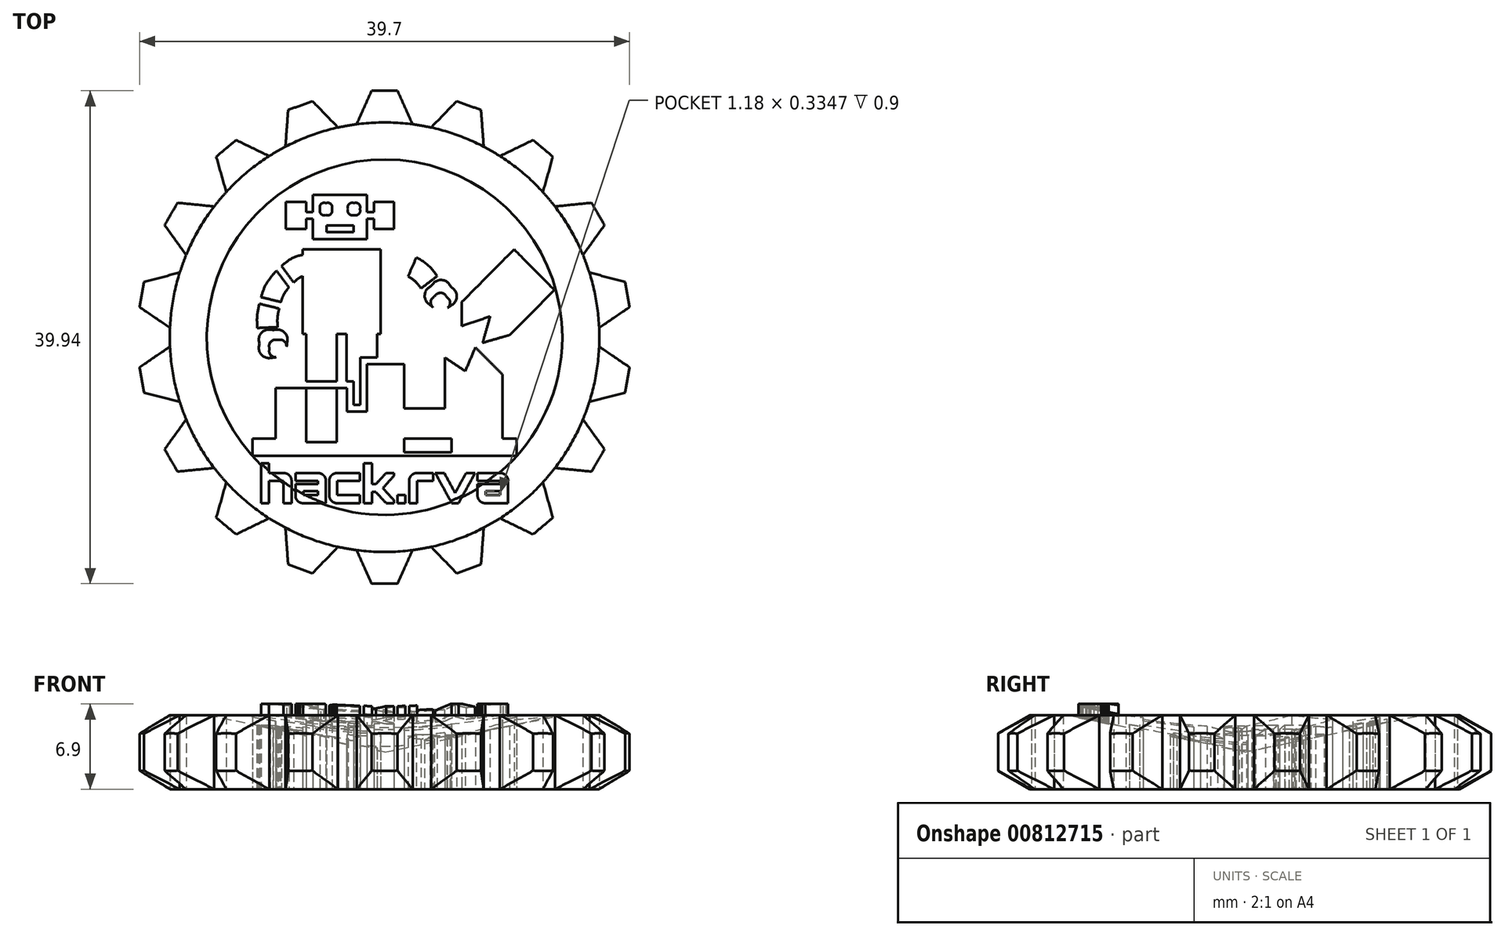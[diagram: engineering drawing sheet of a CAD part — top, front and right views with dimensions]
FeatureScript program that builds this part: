
annotation { "Feature Type Name" : "Feature", "Feature Type Description" : "" }
export const myFeature = defineFeature(function(context is Context, id is Id, definition is map)
    precondition{}
    {
        {
            var Q0;
            Q0=qCreatedBy(makeId("Top.planeOp"),FACE);
            var sketch = newSketch(context, id + "F0", { "sketchPlane" : qUnion([Q0])});
            skCircle(sketch, "E0", {"center": v(0, 0) * mm, "radius": 17.4 * mm, "construction": true});
            skCircle(sketch, "E1", {"center": v(0, 0) * mm, "radius": 20 * mm, "construction": true});
            skLineSegment(sketch, "E2", {"start": v(0, 0) * mm, "end": v(0, 27.02) * mm, "construction": true});
            skLineSegment(sketch, "E3", {"start": v(0, 0) * mm, "end": v(-2.84, 21.54) * mm, "construction": true});
            skLineSegment(sketch, "E4", {"start": v(0, 0) * mm, "end": v(-1.42, 27.06) * mm, "construction": true});
            skPoint(sketch, "E4.endSnap0", {"position": v(-1.42, 10.77) * mm});
            skLineSegment(sketch, "E5", {"start": v(-2.27, 17.25) * mm, "end": v(-1.05, 19.97) * mm});
            skLineSegment(sketch, "E6", {"start": v(-1.05, 19.97) * mm, "end": v(0, 19.97) * mm});
            skLineSegment(sketch, "E7.MirrorCS", {"start": v(2.27, 17.25) * mm, "end": v(1.05, 19.97) * mm});
            skLineSegment(sketch, "E8.MirrorCS", {"start": v(1.05, 19.97) * mm, "end": v(0, 19.97) * mm});
            skLineSegment(sketch, "E9", {"start": v(-2.27, 17.25) * mm, "end": v(2.27, 17.25) * mm});
            skSolve(sketch);
        }
        {
            var Q0;
            Q0=qCreatedBy(makeId("Top.planeOp"),FACE);
            var sketch = newSketch(context, id + "F1", { "sketchPlane" : qUnion([Q0])});
            skCircle(sketch, "E10", {"center": v(0, 0) * mm, "radius": 17.4 * mm});
            skSolve(sketch);
        }
        {
            var Q0;
            Q0=qSketchRegion(id+"F1",true);
            var Q1;
            Q1=qSketchRegion(id+"F0",true);
            extrude(context, id + "F2", {"entities" : qUnion([Q0, Q1]), "depth" : 6 * mm, "offsetDistance" : 25 * mm});
        }
        {
            var Q0;
            Q0=qCreatedBy(makeId("Front.planeOp"),FACE);
            var sketch = newSketch(context, id + "F3", { "sketchPlane" : qUnion([Q0])});
            skLineSegment(sketch, "E11", {"start": v(0, 0) * mm, "end": v(0, 3) * mm});
            skLineSegment(sketch, "E12", {"start": v(0, 3) * mm, "end": v(-14.4, 6) * mm});
            skLineSegment(sketch, "E13", {"start": v(-14.4, 6) * mm, "end": v(-17.4, 6) * mm});
            skLineSegment(sketch, "E14", {"start": v(-17.4, 6) * mm, "end": v(-20, 4.5) * mm});
            skLineSegment(sketch, "E15", {"start": v(-20, 4.5) * mm, "end": v(-20, 1.5) * mm});
            skLineSegment(sketch, "E16", {"start": v(-20, 1.5) * mm, "end": v(-17.4, 0) * mm});
            skLineSegment(sketch, "E17", {"start": v(-17.4, 0) * mm, "end": v(0, 0) * mm});
            skSolve(sketch);
        }
        {
            var Q0;
            Q0=makeQuery(id+"F2.opExtrude","SWEPT_BODY",BODY,{"disambiguationData":[OSD([sQuery(id+"F0.wireOp",EDGE,"E5"),sQuery(id+"F0.wireOp",EDGE,"E6"),sQuery(id+"F0.wireOp",EDGE,"E7.MirrorCS"),sQuery(id+"F0.wireOp",EDGE,"E8.MirrorCS"),sQuery(id+"F0.wireOp",EDGE,"E9")])]});
            var Q1;
            Q1=sQuery(id+"F3.wireOp",EDGE,"E11");
            circularPattern(context, id + "F4", {"operationType" : NewBodyOperationType.ADD, "entities" : qUnion([Q0]), "axis" : qUnion([Q1]), "angle" : 360 * degree, "instanceCount" : 18, "equalSpace" : true});
        }
        {
            var Q0;
            Q0=qCreatedBy(makeId("Top.planeOp"),FACE);
            var sketch = newSketch(context, id + "F5", { "sketchPlane" : qUnion([Q0])});
            skLineSegment(sketch, "E18", {"start": v(7.36, -0.83) * mm, "end": v(6.54, -2.75) * mm});
            skLineSegment(sketch, "E19", {"start": v(6.54, -2.75) * mm, "end": v(4.9, -1.65) * mm});
            skLineSegment(sketch, "E20", {"start": v(4.9, -1.65) * mm, "end": v(4.9, -9.06) * mm});
            skLineSegment(sketch, "E21", {"start": v(4.9, -9.06) * mm, "end": v(9.56, -9.06) * mm});
            skLineSegment(sketch, "E22", {"start": v(9.56, -9.06) * mm, "end": v(9.56, -3.02) * mm});
            skLineSegment(sketch, "E23", {"start": v(9.56, -3.02) * mm, "end": v(8.46, -1.92) * mm});
            skLineSegment(sketch, "E24", {"start": v(8.46, -1.92) * mm, "end": v(7.36, -0.83) * mm});
            skLineSegment(sketch, "E25", {"start": v(1.6, -5.77) * mm, "end": v(5.44, -5.77) * mm});
            skLineSegment(sketch, "E26", {"start": v(5.44, -5.77) * mm, "end": v(5.44, -9.33) * mm});
            skLineSegment(sketch, "E27", {"start": v(5.44, -9.33) * mm, "end": v(1.6, -9.33) * mm});
            skLineSegment(sketch, "E28", {"start": v(1.6, -9.33) * mm, "end": v(1.6, -5.77) * mm});
            skLineSegment(sketch, "E29", {"start": v(8.55, 1.69) * mm, "end": v(7.95, -0.45) * mm});
            skLineSegment(sketch, "E30", {"start": v(7.95, -0.45) * mm, "end": v(10.12, 0.17) * mm});
            skLineSegment(sketch, "E31", {"start": v(10.12, 0.17) * mm, "end": v(13.76, 3.82) * mm});
            skLineSegment(sketch, "E32", {"start": v(13.76, 3.82) * mm, "end": v(10.5, 7.12) * mm});
            skLineSegment(sketch, "E33", {"start": v(10.5, 7.12) * mm, "end": v(6.26, 2.85) * mm});
            skLineSegment(sketch, "E34", {"start": v(6.26, 2.85) * mm, "end": v(6.26, 0.9) * mm});
            skLineSegment(sketch, "E35", {"start": v(6.26, 0.9) * mm, "end": v(8.55, 1.69) * mm});
            skFitSpline(sketch, "E36", {"points": [v(-9.33, -0.94) * mm, v(-9.33, -0.55) * mm, v(-9.02, -0.23) * mm, v(-8.62, -0.23) * mm]});
            skFitSpline(sketch, "E37", {"points": [v(-8.62, -0.23) * mm, v(-8.3, -0.23) * mm, v(-8.02, -0.46) * mm, v(-7.94, -0.77) * mm]});
            skFitSpline(sketch, "E38", {"points": [v(-7.94, -0.77) * mm, v(-7.92, -0.7) * mm, v(-7.91, -0.61) * mm, v(-7.91, -0.53) * mm]});
            skFitSpline(sketch, "E39", {"points": [v(-7.91, -0.53) * mm, v(-7.91, 0.08) * mm, v(-8.41, 0.58) * mm, v(-9.03, 0.58) * mm]});
            skFitSpline(sketch, "E40", {"points": [v(-9.03, 0.58) * mm, v(-9.64, 0.58) * mm, v(-10.14, 0.08) * mm, v(-10.14, -0.53) * mm]});
            skFitSpline(sketch, "E41", {"points": [v(-10.14, -0.53) * mm, v(-10.14, -1.15) * mm, v(-9.64, -1.65) * mm, v(-9.03, -1.65) * mm]});
            skFitSpline(sketch, "E42", {"points": [v(-9.03, -1.65) * mm, v(-8.95, -1.65) * mm, v(-8.87, -1.64) * mm, v(-8.8, -1.63) * mm]});
            skFitSpline(sketch, "E43", {"points": [v(-8.8, -1.63) * mm, v(-9.1, -1.55) * mm, v(-9.33, -1.27) * mm, v(-9.33, -0.94) * mm]});
            skLineSegment(sketch, "E44", {"start": v(-1.42, 10.15) * mm, "end": v(0.77, 10.15) * mm});
            skLineSegment(sketch, "E45", {"start": v(0.77, 10.15) * mm, "end": v(0.77, 9.6) * mm});
            skLineSegment(sketch, "E46", {"start": v(0.77, 9.6) * mm, "end": v(-1.42, 9.6) * mm});
            skLineSegment(sketch, "E47", {"start": v(-1.42, 9.6) * mm, "end": v(-1.42, 10.15) * mm});
            skFitSpline(sketch, "E48", {"points": [v(4.04, 3.29) * mm, v(4.33, 3.55) * mm, v(4.78, 3.53) * mm, v(5.04, 3.24) * mm]});
            skFitSpline(sketch, "E49", {"points": [v(5.04, 3.24) * mm, v(5.27, 3) * mm, v(5.29, 2.64) * mm, v(5.11, 2.38) * mm]});
            skFitSpline(sketch, "E50", {"points": [v(5.11, 2.38) * mm, v(5.18, 2.42) * mm, v(5.24, 2.46) * mm, v(5.3, 2.51) * mm]});
            skFitSpline(sketch, "E51", {"points": [v(5.3, 2.51) * mm, v(5.75, 2.93) * mm, v(5.79, 3.64) * mm, v(5.37, 4.1) * mm]});
            skFitSpline(sketch, "E52", {"points": [v(5.37, 4.1) * mm, v(4.95, 4.55) * mm, v(4.25, 4.58) * mm, v(3.8, 4.16) * mm]});
            skFitSpline(sketch, "E53", {"points": [v(3.8, 4.16) * mm, v(3.34, 3.75) * mm, v(3.3, 3.04) * mm, v(3.72, 2.58) * mm]});
            skFitSpline(sketch, "E54", {"points": [v(3.72, 2.58) * mm, v(3.78, 2.53) * mm, v(3.84, 2.48) * mm, v(3.9, 2.43) * mm]});
            skFitSpline(sketch, "E55", {"points": [v(3.9, 2.43) * mm, v(3.75, 2.71) * mm, v(3.8, 3.07) * mm, v(4.04, 3.29) * mm]});
            skFitSpline(sketch, "E56", {"points": [v(-5.24, 10.39) * mm, v(-5.24, 10.65) * mm, v(-5.02, 10.87) * mm, v(-4.75, 10.87) * mm]});
            skFitSpline(sketch, "E57", {"points": [v(-4.75, 10.87) * mm, v(-4.48, 10.87) * mm, v(-4.26, 10.65) * mm, v(-4.26, 10.39) * mm]});
            skFitSpline(sketch, "E58", {"points": [v(-4.26, 10.39) * mm, v(-4.26, 10.12) * mm, v(-4.48, 9.9) * mm, v(-4.75, 9.9) * mm]});
            skFitSpline(sketch, "E59", {"points": [v(-4.75, 9.9) * mm, v(-5.02, 9.9) * mm, v(-5.24, 10.12) * mm, v(-5.24, 10.39) * mm]});
            skLineSegment(sketch, "E60", {"start": v(-5.81, 11.52) * mm, "end": v(-5.81, 7.95) * mm});
            skLineSegment(sketch, "E61", {"start": v(-5.81, 7.95) * mm, "end": v(-1.42, 7.95) * mm});
            skLineSegment(sketch, "E62", {"start": v(-1.42, 7.95) * mm, "end": v(-1.42, 11.52) * mm});
            skLineSegment(sketch, "E63", {"start": v(-1.42, 11.52) * mm, "end": v(-5.81, 11.52) * mm});
            skFitSpline(sketch, "E64", {"points": [v(-2.48, 9.9) * mm, v(-2.75, 9.9) * mm, v(-2.97, 10.12) * mm, v(-2.97, 10.39) * mm]});
            skFitSpline(sketch, "E65", {"points": [v(-2.97, 10.39) * mm, v(-2.97, 10.65) * mm, v(-2.75, 10.87) * mm, v(-2.48, 10.87) * mm]});
            skFitSpline(sketch, "E66", {"points": [v(-2.48, 10.87) * mm, v(-2.21, 10.87) * mm, v(-2, 10.65) * mm, v(-2, 10.39) * mm]});
            skFitSpline(sketch, "E67", {"points": [v(-2, 10.39) * mm, v(-2, 10.12) * mm, v(-2.21, 9.9) * mm, v(-2.48, 9.9) * mm]});
            skLineSegment(sketch, "E68", {"start": v(-2.52, 8.5) * mm, "end": v(-4.71, 8.5) * mm});
            skLineSegment(sketch, "E69", {"start": v(-4.71, 8.5) * mm, "end": v(-4.71, 9.05) * mm});
            skLineSegment(sketch, "E70", {"start": v(-4.71, 9.05) * mm, "end": v(-2.52, 9.05) * mm});
            skLineSegment(sketch, "E71", {"start": v(-2.52, 9.05) * mm, "end": v(-2.52, 8.5) * mm});
            skLineSegment(sketch, "E72", {"start": v(0.77, 8.78) * mm, "end": v(-0.87, 8.78) * mm});
            skLineSegment(sketch, "E73", {"start": v(-0.87, 8.78) * mm, "end": v(-0.87, 10.97) * mm});
            skLineSegment(sketch, "E74", {"start": v(-0.87, 10.97) * mm, "end": v(0.77, 10.97) * mm});
            skLineSegment(sketch, "E75", {"start": v(0.77, 10.97) * mm, "end": v(0.77, 10.42) * mm});
            skLineSegment(sketch, "E76", {"start": v(0.77, 10.42) * mm, "end": v(0.77, 9.33) * mm});
            skLineSegment(sketch, "E77", {"start": v(0.77, 9.33) * mm, "end": v(0.77, 8.78) * mm});
            skLineSegment(sketch, "E78", {"start": v(-8, 10.15) * mm, "end": v(-5.81, 10.15) * mm});
            skLineSegment(sketch, "E79", {"start": v(-5.81, 10.15) * mm, "end": v(-5.81, 9.6) * mm});
            skLineSegment(sketch, "E80", {"start": v(-5.81, 9.6) * mm, "end": v(-8, 9.6) * mm});
            skLineSegment(sketch, "E81", {"start": v(-8, 9.6) * mm, "end": v(-8, 10.15) * mm});
            skLineSegment(sketch, "E82", {"start": v(-6.36, 8.78) * mm, "end": v(-8, 8.78) * mm});
            skLineSegment(sketch, "E83", {"start": v(-8, 8.78) * mm, "end": v(-8, 9.33) * mm});
            skLineSegment(sketch, "E84", {"start": v(-8, 9.33) * mm, "end": v(-8, 10.42) * mm});
            skLineSegment(sketch, "E85", {"start": v(-8, 10.42) * mm, "end": v(-8, 10.97) * mm});
            skLineSegment(sketch, "E86", {"start": v(-8, 10.97) * mm, "end": v(-6.36, 10.97) * mm});
            skLineSegment(sketch, "E87", {"start": v(-6.36, 10.97) * mm, "end": v(-6.36, 8.78) * mm});
            skLineSegment(sketch, "E88", {"start": v(-6.63, 7.13) * mm, "end": v(-0.32, 7.13) * mm});
            skLineSegment(sketch, "E89", {"start": v(-0.32, 7.13) * mm, "end": v(-0.32, 0.27) * mm});
            skLineSegment(sketch, "E90", {"start": v(-0.32, 0.27) * mm, "end": v(-6.63, 0.27) * mm});
            skLineSegment(sketch, "E91", {"start": v(-6.63, 0.27) * mm, "end": v(-6.63, 7.13) * mm});
            skFitSpline(sketch, "E92", {"points": [v(1.9, 4.93) * mm, v(2.29, 4.69) * mm, v(2.64, 4.36) * mm, v(2.95, 3.95) * mm]});
            skLineSegment(sketch, "E93", {"start": v(1.9, 4.93) * mm, "end": v(2.58, 6.45) * mm});
            skFitSpline(sketch, "E94", {"points": [v(4.26, 4.95) * mm, v(3.78, 5.59) * mm, v(3.2, 6.1) * mm, v(2.58, 6.45) * mm]});
            skLineSegment(sketch, "E95", {"start": v(2.95, 3.95) * mm, "end": v(4.26, 4.95) * mm});
            skLineSegment(sketch, "E96", {"start": v(4.26, 4.95) * mm, "end": v(2.95, 3.95) * mm});
            skFitSpline(sketch, "E97", {"points": [v(-5.82, 6.69) * mm, v(-6.77, 6.65) * mm, v(-7.63, 6.32) * mm, v(-8.34, 5.76) * mm]});
            skFitSpline(sketch, "E98", {"points": [v(-7.37, 4.43) * mm, v(-6.91, 4.8) * mm, v(-6.37, 5.02) * mm, v(-5.75, 5.04) * mm]});
            skFitSpline(sketch, "E99", {"points": [v(-5.75, 5.04) * mm, v(-4.6, 5.1) * mm, v(-3.52, 4.48) * mm, v(-2.78, 3.35) * mm]});
            skLineSegment(sketch, "E100", {"start": v(-8.34, 5.76) * mm, "end": v(-7.37, 4.43) * mm});
            skLineSegment(sketch, "E101", {"start": v(-7.37, 4.43) * mm, "end": v(-8.34, 5.76) * mm});
            skFitSpline(sketch, "E102", {"points": [v(-1.4, 4.25) * mm, v(-2.47, 5.88) * mm, v(-4.08, 6.77) * mm, v(-5.82, 6.69) * mm]});
            skLineSegment(sketch, "E103", {"start": v(-2.78, 3.35) * mm, "end": v(-1.4, 4.25) * mm});
            skLineSegment(sketch, "E104", {"start": v(-1.4, 4.25) * mm, "end": v(-2.78, 3.35) * mm});
            skFitSpline(sketch, "E105", {"points": [v(-10.14, 2.71) * mm, v(-10.28, 2.1) * mm, v(-10.34, 1.43) * mm, v(-10.3, 0.74) * mm]});
            skLineSegment(sketch, "E106", {"start": v(-8.54, 2.32) * mm, "end": v(-10.14, 2.71) * mm});
            skLineSegment(sketch, "E107", {"start": v(-10.14, 2.71) * mm, "end": v(-8.54, 2.32) * mm});
            skFitSpline(sketch, "E108", {"points": [v(-8.66, 0.82) * mm, v(-8.69, 1.35) * mm, v(-8.64, 1.85) * mm, v(-8.54, 2.32) * mm]});
            skLineSegment(sketch, "E109", {"start": v(-10.3, 0.74) * mm, "end": v(-8.66, 0.82) * mm});
            skLineSegment(sketch, "E110", {"start": v(-8.66, 0.82) * mm, "end": v(-10.3, 0.74) * mm});
            skFitSpline(sketch, "E111", {"points": [v(-8.4, 2.85) * mm, v(-8.28, 3.22) * mm, v(-8.12, 3.55) * mm, v(-7.92, 3.84) * mm]});
            skFitSpline(sketch, "E112", {"points": [v(-7.92, 3.84) * mm, v(-7.87, 3.9) * mm, v(-7.81, 3.98) * mm, v(-7.76, 4.04) * mm]});
            skFitSpline(sketch, "E113", {"points": [v(-8.75, 5.39) * mm, v(-8.94, 5.2) * mm, v(-9.11, 5) * mm, v(-9.27, 4.78) * mm]});
            skFitSpline(sketch, "E114", {"points": [v(-9.27, 4.78) * mm, v(-9.58, 4.32) * mm, v(-9.82, 3.8) * mm, v(-10, 3.24) * mm]});
            skLineSegment(sketch, "E115", {"start": v(-7.76, 4.04) * mm, "end": v(-8.75, 5.39) * mm});
            skLineSegment(sketch, "E116", {"start": v(-8.75, 5.39) * mm, "end": v(-7.76, 4.04) * mm});
            skLineSegment(sketch, "E117", {"start": v(-10, 3.24) * mm, "end": v(-8.4, 2.85) * mm});
            skLineSegment(sketch, "E118", {"start": v(-8.4, 2.85) * mm, "end": v(-10, 3.24) * mm});
            skLineSegment(sketch, "E119", {"start": v(1.6, -2.19) * mm, "end": v(-1.43, -2.19) * mm});
            skLineSegment(sketch, "E120", {"start": v(-2.52, -3.57) * mm, "end": v(-2.52, -5.5) * mm});
            skLineSegment(sketch, "E121", {"start": v(-2.52, -5.5) * mm, "end": v(-1.97, -5.5) * mm});
            skLineSegment(sketch, "E122", {"start": v(-0.6, -1.65) * mm, "end": v(-0.6, 1.1) * mm});
            skLineSegment(sketch, "E123", {"start": v(-0.6, 1.1) * mm, "end": v(-3.07, 1.1) * mm});
            skLineSegment(sketch, "E124", {"start": v(-3.07, 1.1) * mm, "end": v(-3.07, -3.57) * mm});
            skLineSegment(sketch, "E125", {"start": v(-3.07, -3.57) * mm, "end": v(-2.52, -3.57) * mm});
            skLineSegment(sketch, "E126", {"start": v(-10.7, -8.23) * mm, "end": v(10.7, -8.23) * mm});
            skLineSegment(sketch, "E127", {"start": v(10.7, -9.6) * mm, "end": v(-10.7, -9.6) * mm});
            skFitSpline(sketch, "E128", {"points": [v(0.02, 5.44) * mm, v(0.53, 5.48) * mm, v(1.02, 5.4) * mm, v(1.5, 5.2) * mm]});
            skLineSegment(sketch, "E129", {"start": v(0.22, 5.45) * mm, "end": v(0.22, 7.1) * mm});
            skFitSpline(sketch, "E130", {"points": [v(2.09, 6.7) * mm, v(1.41, 7) * mm, v(0.7, 7.13) * mm, v(-0.05, 7.09) * mm]});
            skLineSegment(sketch, "E131", {"start": v(1.44, 5.21) * mm, "end": v(2.04, 6.72) * mm});
            skLineSegment(sketch, "E132", {"start": v(-6.36, 1.1) * mm, "end": v(-3.89, 1.1) * mm});
            skLineSegment(sketch, "E133", {"start": v(-3.89, 1.1) * mm, "end": v(-3.89, -3.57) * mm});
            skLineSegment(sketch, "E134", {"start": v(-3.89, -3.57) * mm, "end": v(-6.36, -3.57) * mm});
            skLineSegment(sketch, "E135", {"start": v(-6.36, -3.57) * mm, "end": v(-6.36, 1.1) * mm});
            skLineSegment(sketch, "E136", {"start": v(-6.36, -4.12) * mm, "end": v(-3.89, -4.12) * mm});
            skLineSegment(sketch, "E137", {"start": v(-3.89, -4.12) * mm, "end": v(-3.89, -8.5) * mm});
            skLineSegment(sketch, "E138", {"start": v(-3.89, -8.5) * mm, "end": v(-6.36, -8.5) * mm});
            skLineSegment(sketch, "E139", {"start": v(-6.36, -8.5) * mm, "end": v(-6.36, -4.12) * mm});
            skLineSegment(sketch, "E140", {"start": v(10.7, -8.23) * mm, "end": v(10.7, -9.6) * mm});
            skLineSegment(sketch, "E141", {"start": v(-10.7, -9.6) * mm, "end": v(-10.7, -8.23) * mm});
            skLineSegment(sketch, "E142", {"start": v(-1.43, -2.19) * mm, "end": v(-1.43, -6.03) * mm});
            skLineSegment(sketch, "E143", {"start": v(-1.97, -1.65) * mm, "end": v(-1.97, -5.5) * mm});
            skLineSegment(sketch, "E144", {"start": v(1.6, -2.19) * mm, "end": v(1.6, -8.78) * mm});
            skLineSegment(sketch, "E145", {"start": v(1.6, -8.78) * mm, "end": v(-0.87, -8.78) * mm});
            skLineSegment(sketch, "E146", {"start": v(-0.87, -8.78) * mm, "end": v(-0.87, -9.33) * mm});
            skLineSegment(sketch, "E147", {"start": v(-0.87, -9.33) * mm, "end": v(-2.8, -9.33) * mm});
            skLineSegment(sketch, "E148", {"start": v(-2.8, -9.33) * mm, "end": v(-2.8, -9.6) * mm});
            skLineSegment(sketch, "E149", {"start": v(-2.8, -9.6) * mm, "end": v(-8.83, -9.6) * mm});
            skLineSegment(sketch, "E150", {"start": v(-8.83, -9.6) * mm, "end": v(-8.83, -4.11) * mm});
            skLineSegment(sketch, "E151", {"start": v(-0.6, -1.65) * mm, "end": v(-1.97, -1.65) * mm});
            skLineSegment(sketch, "E152", {"start": v(-3.06, -6.03) * mm, "end": v(-1.43, -6.03) * mm});
            skLineSegment(sketch, "E153", {"start": v(-3.06, -4.11) * mm, "end": v(-3.06, -6.03) * mm});
            skLineSegment(sketch, "E154", {"start": v(-3.06, -4.11) * mm, "end": v(-8.83, -4.11) * mm});
            skSolve(sketch);
        }
        {
            var Q0;
            Q0=qSketchRegion(id+"F5",true);
            var Q1;
            Q1=sQuery(id+"F5.wireOp",EDGE,"6252c9fc-d5b5-40d1-89bb-2a5f3184dae9");
            var Q2;
            Q2=sQuery(id+"F5.wireOp",EDGE,"E90");
            var Q3;
            Q3=sQuery(id+"F5.wireOp",EDGE,"E134");
            var Q4;
            Q4=sQuery(id+"F5.wireOp",EDGE,"E94");
            var Q5;
            Q5=sQuery(id+"F5.wireOp",EDGE,"E130");
            var Q6;
            Q6=sQuery(id+"F5.wireOp",EDGE,"E22");
            var Q7;
            Q7=sQuery(id+"F5.wireOp",EDGE,"E35");
            var Q8;
            Q8=sQuery(id+"F5.wireOp",EDGE,"E28");
            var Q9;
            Q9=sQuery(id+"F5.wireOp",EDGE,"E105");
            var Q10;
            Q10=sQuery(id+"F5.wireOp",EDGE,"95198ed3-3c3b-4ae5-9471-770df729d098");
            var Q11;
            Q11=sQuery(id+"F5.wireOp",EDGE,"E135");
            var Q12;
            Q12=sQuery(id+"F5.wireOp",EDGE,"6b8f1946-e8d9-42c7-b529-401e110b12ef");
            var Q13;
            Q13=sQuery(id+"F5.wireOp",EDGE,"E26");
            var Q14;
            Q14=sQuery(id+"F5.wireOp",EDGE,"E99");
            var Q15;
            Q15=sQuery(id+"F5.wireOp",EDGE,"E20");
            var Q16;
            Q16=sQuery(id+"F5.wireOp",EDGE,"E68");
            var Q17;
            Q17=sQuery(id+"F5.wireOp",EDGE,"E126");
            var Q18;
            Q18=sQuery(id+"F5.wireOp",EDGE,"E124");
            var Q19;
            Q19=sQuery(id+"F5.wireOp",EDGE,"77c6bc89-9393-4709-9f76-2ba73c08c8e3");
            var Q20;
            Q20=sQuery(id+"F5.wireOp",EDGE,"E34");
            var Q21;
            Q21=sQuery(id+"F5.wireOp",EDGE,"E133");
            var Q22;
            Q22=sQuery(id+"F5.wireOp",EDGE,"b3271c8d-d34e-48d3-8350-166866a1ef0d");
            var Q23;
            Q23=sQuery(id+"F5.wireOp",EDGE,"E33");
            var Q24;
            Q24=sQuery(id+"F5.wireOp",EDGE,"E138");
            var Q25;
            Q25=sQuery(id+"F5.wireOp",EDGE,"E21");
            var Q26;
            Q26=sQuery(id+"F5.wireOp",EDGE,"9cf7919e-c9ea-4169-a484-167db1e63cf2");
            var Q27;
            Q27=sQuery(id+"F5.wireOp",EDGE,"E70");
            var Q28;
            Q28=sQuery(id+"F5.wireOp",EDGE,"E18");
            var Q29;
            Q29=sQuery(id+"F5.wireOp",EDGE,"E31");
            var Q30;
            Q30=sQuery(id+"F5.wireOp",EDGE,"E32");
            var Q31;
            Q31=sQuery(id+"F5.wireOp",EDGE,"E27");
            var Q32;
            Q32=sQuery(id+"F5.wireOp",EDGE,"E30");
            var Q33;
            Q33=sQuery(id+"F5.wireOp",EDGE,"E29");
            var Q34;
            Q34=sQuery(id+"F5.wireOp",EDGE,"E139");
            var Q35;
            Q35=sQuery(id+"F5.wireOp",EDGE,"E102");
            var Q36;
            Q36=sQuery(id+"F5.wireOp",EDGE,"E122");
            var Q37;
            Q37=sQuery(id+"F5.wireOp",EDGE,"E119");
            var Q38;
            Q38=sQuery(id+"F5.wireOp",EDGE,"E88");
            var Q39;
            Q39=sQuery(id+"F5.wireOp",EDGE,"E136");
            var Q40;
            Q40=sQuery(id+"F5.wireOp",EDGE,"E97");
            var Q41;
            Q41=sQuery(id+"F5.wireOp",EDGE,"1cbca8c9-4c5e-4ba1-ad6a-0479403318c5");
            var Q42;
            Q42=sQuery(id+"F5.wireOp",EDGE,"E137");
            var Q43;
            Q43=sQuery(id+"F5.wireOp",EDGE,"E25");
            var Q44;
            Q44=sQuery(id+"F5.wireOp",EDGE,"E132");
            var Q45;
            Q45=sQuery(id+"F5.wireOp",EDGE,"501fd35c-810e-4cca-a612-50fbb3c57b8b");
            var Q46;
            Q46=sQuery(id+"F5.wireOp",EDGE,"9599e65c-5a11-434d-bada-090ac9876402");
            var Q47;
            Q47=sQuery(id+"F5.wireOp",EDGE,"E63");
            var Q48;
            Q48=sQuery(id+"F5.wireOp",EDGE,"E91");
            var Q49;
            Q49=sQuery(id+"F5.wireOp",EDGE,"3e5a58c2-594a-425e-9fb5-5e991799c867");
            var Q50;
            Q50=sQuery(id+"F5.wireOp",EDGE,"E89");
            var Q51;
            Q51=sQuery(id+"F5.wireOp",EDGE,"E61");
            var Q52;
            Q52=sQuery(id+"F5.wireOp",EDGE,"E123");
            var Q53;
            Q53=sQuery(id+"F5.wireOp",EDGE,"E127");
            var Q54;
            Q54=sQuery(id+"F5.wireOp",EDGE,"9c611efc-dcd8-4982-9a14-8ccc37464665");
            var Q55;
            Q55=sQuery(id+"F5.wireOp",EDGE,"7958f8ac-3e37-4d8b-9a94-ef8a4a095db0");
            var Q56;
            Q56=sQuery(id+"F5.wireOp",EDGE,"E67");
            var Q57;
            Q57=sQuery(id+"F5.wireOp",EDGE,"a202889e-5133-40a2-9648-54841ea52ae1");
            var Q58;
            Q58=sQuery(id+"F5.wireOp",EDGE,"E51");
            var Q59;
            Q59=sQuery(id+"F5.wireOp",EDGE,"E52");
            var Q60;
            Q60=sQuery(id+"F5.wireOp",EDGE,"E23");
            var Q61;
            Q61=sQuery(id+"F5.wireOp",EDGE,"245d8472-72b8-4d4c-ba14-2023b326ec3c");
            var Q62;
            Q62=sQuery(id+"F5.wireOp",EDGE,"E37");
            var Q63;
            Q63=sQuery(id+"F5.wireOp",EDGE,"E40");
            var Q64;
            Q64=sQuery(id+"F5.wireOp",EDGE,"f73ed668-7d07-4108-ba5a-a0242342d377");
            var Q65;
            Q65=sQuery(id+"F5.wireOp",EDGE,"E56");
            var Q66;
            Q66=sQuery(id+"F5.wireOp",EDGE,"E120");
            var Q67;
            Q67=sQuery(id+"F5.wireOp",EDGE,"9350a63d-57cb-49f3-a7ef-09ff34bb147e");
            var Q68;
            Q68=sQuery(id+"F5.wireOp",EDGE,"E75");
            var Q69;
            Q69=sQuery(id+"F5.wireOp",EDGE,"E38");
            var Q70;
            Q70=sQuery(id+"F5.wireOp",EDGE,"E36");
            var Q71;
            Q71=sQuery(id+"F5.wireOp",EDGE,"E19");
            var Q72;
            Q72=sQuery(id+"F5.wireOp",EDGE,"E114");
            var Q73;
            Q73=sQuery(id+"F5.wireOp",EDGE,"E64");
            var Q74;
            Q74=sQuery(id+"F5.wireOp",EDGE,"7eb34144-0e09-40d5-ad89-3aa24f313f34");
            var Q75;
            Q75=sQuery(id+"F5.wireOp",EDGE,"E62");
            var Q76;
            Q76=sQuery(id+"F5.wireOp",EDGE,"b9910873-99ff-419f-af87-6d7518b8f7e3");
            var Q77;
            Q77=sQuery(id+"F5.wireOp",EDGE,"E66");
            var Q78;
            Q78=sQuery(id+"F5.wireOp",EDGE,"E98");
            var Q79;
            Q79=sQuery(id+"F5.wireOp",EDGE,"E39");
            var Q80;
            Q80=sQuery(id+"F5.wireOp",EDGE,"E24");
            var Q81;
            Q81=sQuery(id+"F5.wireOp",EDGE,"271be0f0-f1cb-4401-a4b2-863b38b25cbf");
            var Q82;
            Q82=sQuery(id+"F5.wireOp",EDGE,"E59");
            var Q83;
            Q83=sQuery(id+"F5.wireOp",EDGE,"E58");
            var Q84;
            Q84=sQuery(id+"F5.wireOp",EDGE,"6881dcda-d3f3-45b8-92d9-aef02fdce9f0");
            var Q85;
            Q85=sQuery(id+"F5.wireOp",EDGE,"80ce520b-dfcc-41bd-b307-2275fff168de");
            var Q86;
            Q86=sQuery(id+"F5.wireOp",EDGE,"E60");
            var Q87;
            Q87=sQuery(id+"F5.wireOp",EDGE,"49f96cd5-bb83-4969-bef7-f8b0555d9afb");
            var Q88;
            Q88=sQuery(id+"F5.wireOp",EDGE,"E50");
            var Q89;
            Q89=sQuery(id+"F5.wireOp",EDGE,"E65");
            var Q90;
            Q90=sQuery(id+"F5.wireOp",EDGE,"E48");
            var Q91;
            Q91=sQuery(id+"F5.wireOp",EDGE,"E76");
            var Q92;
            Q92=sQuery(id+"F5.wireOp",EDGE,"E86");
            var Q93;
            Q93=sQuery(id+"F5.wireOp",EDGE,"E74");
            var Q94;
            Q94=sQuery(id+"F5.wireOp",EDGE,"E121");
            var Q95;
            Q95=sQuery(id+"F5.wireOp",EDGE,"E41");
            var Q96;
            Q96=sQuery(id+"F5.wireOp",EDGE,"E57");
            var Q97;
            Q97=sQuery(id+"F5.wireOp",EDGE,"E73");
            var Q98;
            Q98=sQuery(id+"F5.wireOp",EDGE,"E118");
            var Q99;
            Q99=sQuery(id+"F5.wireOp",EDGE,"E128");
            var Q100;
            Q100=sQuery(id+"F5.wireOp",EDGE,"7a0b8d0e-4b81-4c44-9afd-528a34b3260d");
            var Q101;
            Q101=sQuery(id+"F5.wireOp",EDGE,"7380d2c0-04a1-482f-afdd-3e53df784789");
            var Q102;
            Q102=sQuery(id+"F5.wireOp",EDGE,"E107");
            var Q103;
            Q103=sQuery(id+"F5.wireOp",EDGE,"E108");
            var Q104;
            Q104=sQuery(id+"F5.wireOp",EDGE,"E49");
            var Q105;
            Q105=sQuery(id+"F5.wireOp",EDGE,"E110");
            var Q106;
            Q106=sQuery(id+"F5.wireOp",EDGE,"E96");
            var Q107;
            Q107=sQuery(id+"F5.wireOp",EDGE,"E84");
            var Q108;
            Q108=sQuery(id+"F5.wireOp",EDGE,"E115");
            var Q109;
            Q109=sQuery(id+"F5.wireOp",EDGE,"E101");
            var Q110;
            Q110=sQuery(id+"F5.wireOp",EDGE,"E44");
            var Q111;
            Q111=sQuery(id+"F5.wireOp",EDGE,"E53");
            var Q112;
            Q112=sQuery(id+"F5.wireOp",EDGE,"E112");
            var Q113;
            Q113=sQuery(id+"F5.wireOp",EDGE,"bea348f1-2834-486b-88b8-9efe3fc24a35");
            var Q114;
            Q114=sQuery(id+"F5.wireOp",EDGE,"E113");
            var Q115;
            Q115=sQuery(id+"F5.wireOp",EDGE,"E111");
            var Q116;
            Q116=sQuery(id+"F5.wireOp",EDGE,"E93");
            var Q117;
            Q117=sQuery(id+"F5.wireOp",EDGE,"E92");
            var Q118;
            Q118=sQuery(id+"F5.wireOp",EDGE,"E104");
            var Q119;
            Q119=sQuery(id+"F5.wireOp",EDGE,"E129");
            var Q120;
            Q120=sQuery(id+"F5.wireOp",EDGE,"E81");
            var Q121;
            Q121=sQuery(id+"F5.wireOp",EDGE,"E82");
            var Q122;
            Q122=sQuery(id+"F5.wireOp",EDGE,"E131");
            var Q123;
            Q123=sQuery(id+"F5.wireOp",EDGE,"E78");
            var Q124;
            Q124=sQuery(id+"F5.wireOp",EDGE,"2920f785-dd79-45f9-bf60-775b209ab1aa");
            var Q125;
            Q125=sQuery(id+"F5.wireOp",EDGE,"E71");
            var Q126;
            Q126=sQuery(id+"F5.wireOp",EDGE,"E72");
            var Q127;
            Q127=sQuery(id+"F5.wireOp",EDGE,"E95");
            var Q128;
            Q128=sQuery(id+"F5.wireOp",EDGE,"E106");
            var Q129;
            Q129=sQuery(id+"F5.wireOp",EDGE,"4508b117-1b24-4e03-9ee8-5eba73059b6f");
            var Q130;
            Q130=sQuery(id+"F5.wireOp",EDGE,"E46");
            var Q131;
            Q131=sQuery(id+"F5.wireOp",EDGE,"E79");
            var Q132;
            Q132=sQuery(id+"F5.wireOp",EDGE,"E109");
            var Q133;
            Q133=sQuery(id+"F5.wireOp",EDGE,"E83");
            var Q134;
            Q134=sQuery(id+"F5.wireOp",EDGE,"E55");
            var Q135;
            Q135=sQuery(id+"F5.wireOp",EDGE,"E117");
            var Q136;
            Q136=sQuery(id+"F5.wireOp",EDGE,"E103");
            var Q137;
            Q137=sQuery(id+"F5.wireOp",EDGE,"59ec6001-5882-40ab-8e6c-5c3990616cf8");
            var Q138;
            Q138=sQuery(id+"F5.wireOp",EDGE,"E69");
            var Q139;
            Q139=sQuery(id+"F5.wireOp",EDGE,"3ce1abf4-0037-43e6-ac3b-050355aa1771");
            var Q140;
            Q140=sQuery(id+"F5.wireOp",EDGE,"E80");
            var Q141;
            Q141=sQuery(id+"F5.wireOp",EDGE,"E125");
            var Q142;
            Q142=sQuery(id+"F5.wireOp",EDGE,"E47");
            var Q143;
            Q143=sQuery(id+"F5.wireOp",EDGE,"E77");
            var Q144;
            Q144=sQuery(id+"F5.wireOp",EDGE,"E45");
            var Q145;
            Q145=sQuery(id+"F5.wireOp",EDGE,"E87");
            var Q146;
            Q146=sQuery(id+"F5.wireOp",EDGE,"E43");
            var Q147;
            Q147=sQuery(id+"F5.wireOp",EDGE,"E85");
            var Q148;
            Q148=sQuery(id+"F5.wireOp",EDGE,"E100");
            var Q149;
            Q149=sQuery(id+"F5.wireOp",EDGE,"E116");
            var Q150;
            Q150=sQuery(id+"F5.wireOp",EDGE,"E54");
            var Q151;
            Q151=sQuery(id+"F5.wireOp",EDGE,"E42");
            extrude(context, id + "F6", {"entities" : qUnion([Q0]), "operationType" : NewBodyOperationType.REMOVE, "surfaceEntities" : qUnion([Q1, Q2, Q3, Q4, Q5, Q6, Q7, Q8, Q9, Q10, Q11, Q12, Q13, Q14, Q15, Q16, Q17, Q18, Q19, Q20, Q21, Q22, Q23, Q24, Q25, Q26, Q27, Q28, Q29, Q30, Q31, Q32, Q33, Q34, Q35, Q36, Q37, Q38, Q39, Q40, Q41, Q42, Q43, Q44, Q45, Q46, Q47, Q48, Q49, Q50, Q51, Q52, Q53, Q54, Q55, Q56, Q57, Q58, Q59, Q60, Q61, Q62, Q63, Q64, Q65, Q66, Q67, Q68, Q69, Q70, Q71, Q72, Q73, Q74, Q75, Q76, Q77, Q78, Q79, Q80, Q81, Q82, Q83, Q84, Q85, Q86, Q87, Q88, Q89, Q90, Q91, Q92, Q93, Q94, Q95, Q96, Q97, Q98, Q99, Q100, Q101, Q102, Q103, Q104, Q105, Q106, Q107, Q108, Q109, Q110, Q111, Q112, Q113, Q114, Q115, Q116, Q117, Q118, Q119, Q120, Q121, Q122, Q123, Q124, Q125, Q126, Q127, Q128, Q129, Q130, Q131, Q132, Q133, Q134, Q135, Q136, Q137, Q138, Q139, Q140, Q141, Q142, Q143, Q144, Q145, Q146, Q147, Q148, Q149, Q150, Q151]), "depth" : 6 * mm, "offsetDistance" : 25 * mm});
        }
        {
            var Q0;
            Q0=qSketchRegion(id+"F3",true);
            var Q1;
            Q1=sQuery(id+"F3.wireOp",EDGE,"E11");
            revolve(context, id + "F7", {"operationType" : NewBodyOperationType.INTERSECT, "surfaceOperationType" : NewSurfaceOperationType.NEW, "entities" : qUnion([Q0]), "axis" : qUnion([Q1]), "revolveType" : RevolveType.FULL});
        }
        {
            var Q0;
            {var subQ16=sQuery(id+"F0.wireOp",EDGE,"E8.MirrorCS");var subQ17=sQuery(id+"F0.wireOp",EDGE,"E6");var subQ19=sQuery(id+"F0.wireOp",EDGE,"E5");var subQ20=makeQuery(id+"F2.opExtrude","SWEPT_FACE",FACE,{"disambiguationData":[OSD([subQ19])]});var subQ21=sQuery(id+"F0.wireOp",EDGE,"E7.MirrorCS");var subQ25=sQuery(id+"F1.wireOp",EDGE,"E10");var subQ59=makeQuery(id+"F2.opExtrude","CAP_FACE",FACE,{"disambiguationData":[OSD([subQ19,subQ17,subQ21,subQ16,sQuery(id+"F0.wireOp",EDGE,"E9")])],"isStart":false});Q0=makeQuery(id+"F6.boolean.opBoolean","SPLIT",FACE,{"disambiguationData":[TD([subQ20])],"derivedFrom":makeQuery(id+"F4.boolean.opBoolean","MERGE",FACE,{"derivedFrom":[subQ59,makeQuery(id+"F2.opExtrude","CAP_FACE",FACE,{"disambiguationData":[OSD([subQ25])],"isStart":false}),makeQuery(id+"F4.opPattern","COPY",FACE,{"derivedFrom":subQ59,"instanceName":"1"}),makeQuery(id+"F4.opPattern","COPY",FACE,{"derivedFrom":subQ59,"instanceName":"2"}),makeQuery(id+"F4.opPattern","COPY",FACE,{"derivedFrom":subQ59,"instanceName":"3"}),makeQuery(id+"F4.opPattern","COPY",FACE,{"derivedFrom":subQ59,"instanceName":"4"}),makeQuery(id+"F4.opPattern","COPY",FACE,{"derivedFrom":subQ59,"instanceName":"5"}),makeQuery(id+"F4.opPattern","COPY",FACE,{"derivedFrom":subQ59,"instanceName":"6"}),makeQuery(id+"F4.opPattern","COPY",FACE,{"derivedFrom":subQ59,"instanceName":"7"}),makeQuery(id+"F4.opPattern","COPY",FACE,{"derivedFrom":subQ59,"instanceName":"8"}),makeQuery(id+"F4.opPattern","COPY",FACE,{"derivedFrom":subQ59,"instanceName":"9"}),makeQuery(id+"F4.opPattern","COPY",FACE,{"derivedFrom":subQ59,"instanceName":"10"}),makeQuery(id+"F4.opPattern","COPY",FACE,{"derivedFrom":subQ59,"instanceName":"11"}),makeQuery(id+"F4.opPattern","COPY",FACE,{"derivedFrom":subQ59,"instanceName":"12"}),makeQuery(id+"F4.opPattern","COPY",FACE,{"derivedFrom":subQ59,"instanceName":"13"}),makeQuery(id+"F4.opPattern","COPY",FACE,{"derivedFrom":subQ59,"instanceName":"14"}),makeQuery(id+"F4.opPattern","COPY",FACE,{"derivedFrom":subQ59,"instanceName":"15"}),makeQuery(id+"F4.opPattern","COPY",FACE,{"derivedFrom":subQ59,"instanceName":"16"}),makeQuery(id+"F4.opPattern","COPY",FACE,{"derivedFrom":subQ59,"instanceName":"17"})]})});}
            cPlane(context, id + "F8", {"entities" : qUnion([Q0]), "cplaneType" : CPlaneType.OFFSET, "offset" : 0 * mm, "width" : 150 * mm, "height" : 150 * mm});
        }
        {
            var Q0;
            Q0=qCreatedBy(makeId("Top.planeOp"),FACE);
            var sketch = newSketch(context, id + "F9", { "sketchPlane" : qUnion([Q0])});
            skFitSpline(sketch, "E155", {"points": [v(-8.15, -11.01) * mm, v(-8.06, -11.01) * mm, v(-7.98, -11.03) * mm, v(-7.91, -11.06) * mm]});
            skFitSpline(sketch, "E156", {"points": [v(-7.91, -11.06) * mm, v(-7.84, -11.1) * mm, v(-7.78, -11.14) * mm, v(-7.72, -11.2) * mm]});
            skFitSpline(sketch, "E157", {"points": [v(-7.72, -11.2) * mm, v(-7.66, -11.25) * mm, v(-7.62, -11.31) * mm, v(-7.59, -11.39) * mm]});
            skFitSpline(sketch, "E158", {"points": [v(-7.59, -11.39) * mm, v(-7.56, -11.46) * mm, v(-7.54, -11.54) * mm, v(-7.54, -11.62) * mm]});
            skFitSpline(sketch, "E159", {"points": [v(-5.37, -11.01) * mm, v(-5.28, -11.01) * mm, v(-5.2, -11.03) * mm, v(-5.13, -11.06) * mm]});
            skFitSpline(sketch, "E160", {"points": [v(-5.13, -11.06) * mm, v(-5.06, -11.1) * mm, v(-5, -11.14) * mm, v(-4.94, -11.2) * mm]});
            skFitSpline(sketch, "E161", {"points": [v(-4.94, -11.2) * mm, v(-4.88, -11.25) * mm, v(-4.84, -11.31) * mm, v(-4.81, -11.39) * mm]});
            skFitSpline(sketch, "E162", {"points": [v(-4.81, -11.39) * mm, v(-4.78, -11.46) * mm, v(-4.76, -11.54) * mm, v(-4.76, -11.62) * mm]});
            skLineSegment(sketch, "E163", {"start": v(-7.54, -11.62) * mm, "end": v(-7.54, -13.44) * mm});
            skLineSegment(sketch, "E164", {"start": v(-7.54, -13.44) * mm, "end": v(-8.18, -13.44) * mm});
            skLineSegment(sketch, "E165", {"start": v(-8.18, -13.44) * mm, "end": v(-8.18, -11.65) * mm});
            skLineSegment(sketch, "E166", {"start": v(-8.18, -11.65) * mm, "end": v(-9.36, -11.65) * mm});
            skLineSegment(sketch, "E167", {"start": v(-9.36, -11.65) * mm, "end": v(-9.36, -13.44) * mm});
            skLineSegment(sketch, "E168", {"start": v(-9.36, -13.44) * mm, "end": v(-10, -13.44) * mm});
            skLineSegment(sketch, "E169", {"start": v(-10, -13.44) * mm, "end": v(-10, -10.22) * mm});
            skLineSegment(sketch, "E170", {"start": v(-10, -10.22) * mm, "end": v(-9.36, -10.22) * mm});
            skLineSegment(sketch, "E171", {"start": v(-9.36, -10.22) * mm, "end": v(-9.36, -11.01) * mm});
            skLineSegment(sketch, "E172", {"start": v(-9.36, -11.01) * mm, "end": v(-8.15, -11.01) * mm});
            skFitSpline(sketch, "E173", {"points": [v(-6.61, -13.44) * mm, v(-6.7, -13.44) * mm, v(-6.78, -13.43) * mm, v(-6.85, -13.4) * mm]});
            skFitSpline(sketch, "E174", {"points": [v(-6.85, -13.4) * mm, v(-6.93, -13.36) * mm, v(-6.99, -13.32) * mm, v(-7.05, -13.26) * mm]});
            skFitSpline(sketch, "E175", {"points": [v(-7.05, -13.26) * mm, v(-7.1, -13.2) * mm, v(-7.14, -13.14) * mm, v(-7.18, -13.07) * mm]});
            skFitSpline(sketch, "E176", {"points": [v(-7.18, -13.07) * mm, v(-7.2, -13) * mm, v(-7.22, -12.92) * mm, v(-7.22, -12.83) * mm]});
            skLineSegment(sketch, "E177", {"start": v(-4.76, -11.62) * mm, "end": v(-4.76, -13.44) * mm});
            skLineSegment(sketch, "E178", {"start": v(-4.76, -13.44) * mm, "end": v(-6.61, -13.44) * mm});
            skLineSegment(sketch, "E179", {"start": v(-7.22, -12.83) * mm, "end": v(-7.22, -11.9) * mm});
            skLineSegment(sketch, "E180", {"start": v(-7.22, -11.9) * mm, "end": v(-5.4, -11.9) * mm});
            skLineSegment(sketch, "E181", {"start": v(-5.4, -11.9) * mm, "end": v(-5.4, -11.65) * mm});
            skLineSegment(sketch, "E182", {"start": v(-5.4, -11.65) * mm, "end": v(-7.22, -11.65) * mm});
            skLineSegment(sketch, "E183", {"start": v(-7.22, -11.65) * mm, "end": v(-7.22, -11.01) * mm});
            skLineSegment(sketch, "E184", {"start": v(-7.22, -11.01) * mm, "end": v(-5.37, -11.01) * mm});
            skLineSegment(sketch, "E185", {"start": v(-5.4, -12.47) * mm, "end": v(-6.58, -12.47) * mm});
            skLineSegment(sketch, "E186", {"start": v(-6.58, -12.47) * mm, "end": v(-6.58, -12.8) * mm});
            skLineSegment(sketch, "E187", {"start": v(-6.58, -12.8) * mm, "end": v(-5.4, -12.8) * mm});
            skLineSegment(sketch, "E188", {"start": v(-5.4, -12.8) * mm, "end": v(-5.4, -12.47) * mm});
            skFitSpline(sketch, "E189", {"points": [v(-3.86, -13.44) * mm, v(-3.95, -13.44) * mm, v(-4.03, -13.43) * mm, v(-4.1, -13.4) * mm]});
            skFitSpline(sketch, "E190", {"points": [v(-4.1, -13.4) * mm, v(-4.17, -13.36) * mm, v(-4.24, -13.32) * mm, v(-4.3, -13.26) * mm]});
            skFitSpline(sketch, "E191", {"points": [v(-4.3, -13.26) * mm, v(-4.35, -13.2) * mm, v(-4.4, -13.14) * mm, v(-4.43, -13.07) * mm]});
            skFitSpline(sketch, "E192", {"points": [v(-4.43, -13.07) * mm, v(-4.46, -13) * mm, v(-4.47, -12.92) * mm, v(-4.47, -12.83) * mm]});
            skLineSegment(sketch, "E193", {"start": v(-3.83, -11.65) * mm, "end": v(-3.83, -12.8) * mm});
            skLineSegment(sketch, "E194", {"start": v(-3.83, -12.8) * mm, "end": v(-2.01, -12.8) * mm});
            skLineSegment(sketch, "E195", {"start": v(-2.01, -12.8) * mm, "end": v(-2.01, -13.44) * mm});
            skLineSegment(sketch, "E196", {"start": v(-2.01, -13.44) * mm, "end": v(-3.86, -13.44) * mm});
            skFitSpline(sketch, "E197", {"points": [v(-4.47, -11.62) * mm, v(-4.47, -11.54) * mm, v(-4.46, -11.46) * mm, v(-4.43, -11.39) * mm]});
            skFitSpline(sketch, "E198", {"points": [v(-4.43, -11.39) * mm, v(-4.4, -11.31) * mm, v(-4.35, -11.25) * mm, v(-4.3, -11.2) * mm]});
            skFitSpline(sketch, "E199", {"points": [v(-4.3, -11.2) * mm, v(-4.24, -11.14) * mm, v(-4.17, -11.1) * mm, v(-4.1, -11.06) * mm]});
            skFitSpline(sketch, "E200", {"points": [v(-4.1, -11.06) * mm, v(-4.03, -11.03) * mm, v(-3.95, -11.01) * mm, v(-3.86, -11.01) * mm]});
            skLineSegment(sketch, "E201", {"start": v(-4.47, -12.83) * mm, "end": v(-4.47, -11.62) * mm});
            skLineSegment(sketch, "E202", {"start": v(-4.47, -11.62) * mm, "end": v(-4.47, -12.83) * mm});
            skLineSegment(sketch, "E203", {"start": v(-3.86, -11.01) * mm, "end": v(-2.01, -11.01) * mm});
            skLineSegment(sketch, "E204", {"start": v(-2.01, -11.01) * mm, "end": v(-2.01, -11.65) * mm});
            skLineSegment(sketch, "E205", {"start": v(-2.01, -11.65) * mm, "end": v(-3.83, -11.65) * mm});
            skLineSegment(sketch, "E206", {"start": v(0.76, -11.01) * mm, "end": v(0.76, -11.23) * mm});
            skLineSegment(sketch, "E207", {"start": v(0.76, -11.23) * mm, "end": v(-0.14, -12.23) * mm});
            skLineSegment(sketch, "E208", {"start": v(-0.14, -12.23) * mm, "end": v(0.76, -13.22) * mm});
            skLineSegment(sketch, "E209", {"start": v(0.76, -13.22) * mm, "end": v(0.76, -13.44) * mm});
            skLineSegment(sketch, "E210", {"start": v(0.76, -13.44) * mm, "end": v(0.12, -13.44) * mm});
            skLineSegment(sketch, "E211", {"start": v(0.12, -13.44) * mm, "end": v(-0.7, -12.55) * mm});
            skLineSegment(sketch, "E212", {"start": v(-0.7, -12.55) * mm, "end": v(-1.03, -12.55) * mm});
            skLineSegment(sketch, "E213", {"start": v(-1.03, -12.55) * mm, "end": v(-1.03, -13.44) * mm});
            skLineSegment(sketch, "E214", {"start": v(-1.03, -13.44) * mm, "end": v(-1.67, -13.44) * mm});
            skLineSegment(sketch, "E215", {"start": v(-1.67, -13.44) * mm, "end": v(-1.67, -10.22) * mm});
            skLineSegment(sketch, "E216", {"start": v(-1.67, -10.22) * mm, "end": v(-1.03, -10.22) * mm});
            skLineSegment(sketch, "E217", {"start": v(-1.03, -10.22) * mm, "end": v(-1.03, -11.9) * mm});
            skLineSegment(sketch, "E218", {"start": v(-1.03, -11.9) * mm, "end": v(-0.7, -11.9) * mm});
            skLineSegment(sketch, "E219", {"start": v(-0.7, -11.9) * mm, "end": v(0.12, -11.01) * mm});
            skLineSegment(sketch, "E220", {"start": v(0.12, -11.01) * mm, "end": v(0.76, -11.01) * mm});
            skLineSegment(sketch, "E221", {"start": v(1.67, -13.44) * mm, "end": v(1.03, -13.44) * mm});
            skLineSegment(sketch, "E222", {"start": v(1.03, -13.44) * mm, "end": v(1.03, -12.8) * mm});
            skLineSegment(sketch, "E223", {"start": v(1.03, -12.8) * mm, "end": v(1.67, -12.8) * mm});
            skLineSegment(sketch, "E224", {"start": v(1.67, -12.8) * mm, "end": v(1.67, -13.44) * mm});
            skFitSpline(sketch, "E225", {"points": [v(2, -11.62) * mm, v(2, -11.54) * mm, v(2.01, -11.46) * mm, v(2.04, -11.39) * mm]});
            skFitSpline(sketch, "E226", {"points": [v(2.04, -11.39) * mm, v(2.08, -11.31) * mm, v(2.12, -11.25) * mm, v(2.18, -11.2) * mm]});
            skFitSpline(sketch, "E227", {"points": [v(2.18, -11.2) * mm, v(2.23, -11.14) * mm, v(2.3, -11.1) * mm, v(2.37, -11.06) * mm]});
            skFitSpline(sketch, "E228", {"points": [v(2.37, -11.06) * mm, v(2.45, -11.03) * mm, v(2.53, -11.01) * mm, v(2.6, -11.01) * mm]});
            skLineSegment(sketch, "E229", {"start": v(3.95, -11.01) * mm, "end": v(3.95, -11.65) * mm});
            skLineSegment(sketch, "E230", {"start": v(3.95, -11.65) * mm, "end": v(2.64, -11.65) * mm});
            skLineSegment(sketch, "E231", {"start": v(2.64, -11.65) * mm, "end": v(2.64, -13.44) * mm});
            skLineSegment(sketch, "E232", {"start": v(2.64, -13.44) * mm, "end": v(2, -13.44) * mm});
            skLineSegment(sketch, "E233", {"start": v(2, -13.44) * mm, "end": v(2, -11.62) * mm});
            skLineSegment(sketch, "E234", {"start": v(2.6, -11.01) * mm, "end": v(3.95, -11.01) * mm});
            skLineSegment(sketch, "E235", {"start": v(3.95, -11.01) * mm, "end": v(2.6, -11.01) * mm});
            skFitSpline(sketch, "E236", {"points": [v(9.4, -11.01) * mm, v(9.48, -11.01) * mm, v(9.56, -11.03) * mm, v(9.63, -11.06) * mm]});
            skFitSpline(sketch, "E237", {"points": [v(9.63, -11.06) * mm, v(9.7, -11.1) * mm, v(9.77, -11.14) * mm, v(9.82, -11.2) * mm]});
            skFitSpline(sketch, "E238", {"points": [v(9.82, -11.2) * mm, v(9.88, -11.25) * mm, v(9.92, -11.31) * mm, v(9.95, -11.39) * mm]});
            skFitSpline(sketch, "E239", {"points": [v(9.95, -11.39) * mm, v(9.98, -11.46) * mm, v(10, -11.54) * mm, v(10, -11.62) * mm]});
            skLineSegment(sketch, "E240", {"start": v(7.33, -11.01) * mm, "end": v(6, -13.44) * mm});
            skLineSegment(sketch, "E241", {"start": v(6, -13.44) * mm, "end": v(5.44, -13.44) * mm});
            skLineSegment(sketch, "E242", {"start": v(5.44, -13.44) * mm, "end": v(4.1, -11.01) * mm});
            skLineSegment(sketch, "E243", {"start": v(4.1, -11.01) * mm, "end": v(4.84, -11.01) * mm});
            skLineSegment(sketch, "E244", {"start": v(4.84, -11.01) * mm, "end": v(5.72, -12.63) * mm});
            skLineSegment(sketch, "E245", {"start": v(5.72, -12.63) * mm, "end": v(6.6, -11.01) * mm});
            skLineSegment(sketch, "E246", {"start": v(6.6, -11.01) * mm, "end": v(7.33, -11.01) * mm});
            skFitSpline(sketch, "E247", {"points": [v(8.15, -13.44) * mm, v(8.06, -13.44) * mm, v(7.98, -13.43) * mm, v(7.9, -13.4) * mm]});
            skFitSpline(sketch, "E248", {"points": [v(7.9, -13.4) * mm, v(7.84, -13.36) * mm, v(7.77, -13.32) * mm, v(7.72, -13.26) * mm]});
            skFitSpline(sketch, "E249", {"points": [v(7.72, -13.26) * mm, v(7.66, -13.2) * mm, v(7.62, -13.14) * mm, v(7.59, -13.07) * mm]});
            skFitSpline(sketch, "E250", {"points": [v(7.59, -13.07) * mm, v(7.55, -13) * mm, v(7.54, -12.92) * mm, v(7.54, -12.83) * mm]});
            skLineSegment(sketch, "E251", {"start": v(10, -11.62) * mm, "end": v(10, -13.44) * mm});
            skLineSegment(sketch, "E252", {"start": v(10, -13.44) * mm, "end": v(8.15, -13.44) * mm});
            skLineSegment(sketch, "E253", {"start": v(7.54, -12.83) * mm, "end": v(7.54, -11.9) * mm});
            skLineSegment(sketch, "E254", {"start": v(7.54, -11.9) * mm, "end": v(9.36, -11.9) * mm});
            skLineSegment(sketch, "E255", {"start": v(9.36, -11.9) * mm, "end": v(9.36, -11.65) * mm});
            skLineSegment(sketch, "E256", {"start": v(9.36, -11.65) * mm, "end": v(7.54, -11.65) * mm});
            skLineSegment(sketch, "E257", {"start": v(7.54, -11.65) * mm, "end": v(7.54, -11.01) * mm});
            skLineSegment(sketch, "E258", {"start": v(7.54, -11.01) * mm, "end": v(9.4, -11.01) * mm});
            skLineSegment(sketch, "E259", {"start": v(9.36, -12.47) * mm, "end": v(8.18, -12.47) * mm});
            skLineSegment(sketch, "E260", {"start": v(8.18, -12.47) * mm, "end": v(8.18, -12.8) * mm});
            skLineSegment(sketch, "E261", {"start": v(8.18, -12.8) * mm, "end": v(9.36, -12.8) * mm});
            skLineSegment(sketch, "E262", {"start": v(9.36, -12.8) * mm, "end": v(9.36, -12.47) * mm});
            skSolve(sketch);
        }
        {
            var Q0;
            Q0=qSketchRegion(id+"F9",true);
            extrude(context, id + "F10", {"entities" : qUnion([Q0]), "operationType" : NewBodyOperationType.ADD, "depth" : 7 * mm, "offsetDistance" : 25 * mm});
        }
        {
            var Q0;
            Q0=qCreatedBy(makeId("Front.planeOp"),FACE);
            var sketch = newSketch(context, id + "F11", { "sketchPlane" : qUnion([Q0])});
            skLineSegment(sketch, "E263", {"start": v(-17.4, 6.9) * mm, "end": v(-14.3, 6.9) * mm});
            skLineSegment(sketch, "E264", {"start": v(-14.3, 6.9) * mm, "end": v(0, 3.92) * mm});
            skLineSegment(sketch, "E265", {"start": v(0, 3.92) * mm, "end": v(0, 9.9) * mm});
            skLineSegment(sketch, "E266", {"start": v(0, 9.9) * mm, "end": v(-17.4, 9.9) * mm});
            skLineSegment(sketch, "E267", {"start": v(-17.4, 9.9) * mm, "end": v(-17.4, 6.9) * mm});
            skSolve(sketch);
        }
        {
            var Q0;
            Q0=qSketchRegion(id+"F11",true);
            var Q1;
            Q1=sQuery(id+"F11.wireOp",EDGE,"E265");
            revolve(context, id + "F12", {"operationType" : NewBodyOperationType.REMOVE, "surfaceOperationType" : NewSurfaceOperationType.NEW, "entities" : qUnion([Q0]), "axis" : qUnion([Q1]), "revolveType" : RevolveType.FULL, "oppositeDirection" : true});
        }
    });
